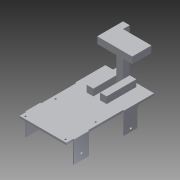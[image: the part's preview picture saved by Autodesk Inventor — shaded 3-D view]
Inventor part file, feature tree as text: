
AUTODESK INVENTOR PART (.ipt)
format: ipt  version: 2014 (Build 180170000, 170)  size: 269,824 bytes
history: native  units: mm
features: sketch x19, extrude x17, plane x4, mirror x3
ambient origin geometry x8: Origin, YZ Plane, XZ Plane, XY Plane, X Axis, Y Axis, Z Axis, Center Point
bodies: Solid1 (feature_tree)
feature tree (43):
  extrude  "Extrusion1"  Depth=20.0mm
  extrude  "Extrusion2"  Depth=20.0mm
  plane  "Work Plane1"
  mirror  "Mirror1"
  extrude  "Extrusion3"  [1 undecoded]
  extrude  "Extrusion10"  Depth=150.0mm
  sketch  "Sketch13"  dims[d26=20.0mm d28=90.0mm d29=20.0mm d31=120.0mm d34=36.0mm d35=0.0mm]
  sketch  "Sketch14"  dims[d36=55.0mm d39=120.0mm]
  plane  "Work Plane2"
  extrude  "Extrusion12"  Depth=20.0mm TaperAngle=0.0deg
  mirror  "Mirror3"
  sketch  "Sketch15"  dims[d44=7.0mm d45=20.0mm]
  extrude  "Extrusion13"  Depth=120.0mm
  mirror  "Mirror4"
  extrude  "Extrusion14"  Depth=20.0mm
  extrude  "Extrusion15"  Depth=65.0mm
  extrude  "Extrusion16"  Depth=7.0mm
  extrude  "Extrusion17"  Depth=3.0mm TaperAngle=0.0deg
  extrude  "Extrusion20"  Depth=10.0mm TaperAngle=0.0deg
  extrude  "Extrusion21"  Depth=50.0mm TaperAngle=0.0deg
  extrude  "Extrusion22"  Depth=50.0mm TaperAngle=0.0deg
  extrude  "Extrusion23"  Depth=20.0mm TaperAngle=0.0deg
  plane  "Work Plane3"
  extrude  "Extrusion24"  Depth=85.0mm TaperAngle=0.0deg
  plane  "Work Plane4"
  extrude  "Extrusion26"  Depth=3.0mm TaperAngle=0.0deg
  extrude  "Extrusion27"  Depth=20.0mm
  sketch  "Sketch2"  dims[d0=20.0mm d1=20.0mm]
  sketch  "Sketch3"  dims[d2=210.0mm d3=0.0mm d4=20.0mm]
  sketch  "Sketch4"  dims[d5=100.0mm d6=0.0mm d7=-50.0mm]
  sketch  "Sketch11"  dims[d9=150.0mm d10=0.0mm d25=5.0mm]
  sketch  "Sketch18"  dims[d47=3.0mm d48=0.0mm d51=65.0mm]
  sketch  "Sketch19"  dims[d52=3.0mm d53=0.0mm d54=7.0mm]
  sketch  "Sketch20"  dims[d55=10.0mm d56=3.0mm d57=0.0mm]
  sketch  "Sketch21"  dims[d58=10.0mm d59=0.0mm d60=10.0mm d61=0.0mm]
  sketch  "Sketch22"  dims[d62=3.0mm d63=0.0mm d71=50.0mm d72=0.0mm]
  sketch  "Sketch25"  dims[d73=3.0mm d74=50.0mm d75=0.0mm]
  sketch  "Sketch26"  dims[d76=40.0mm d77=0.0mm d78=20.0mm d79=0.0mm]
  sketch  "Sketch27"  dims[d80=20.0mm d81=0.0mm d87=85.0mm d88=0.0mm]
  sketch  "Sketch28"  dims[d89=3.0mm d90=5.0mm d91=0.0mm]
  sketch  "Sketch29"  dims[d92=10.0mm d93=20.0mm]
  sketch  "Sketch32"  dims[d94=22.5mm]
  sketch  "Sketch34"
note: 1 required parameter value undecoded (feature->parameter linkage not recoverable at this tier; creation-order binding heuristic only, values carry confidence <= 0.55)
